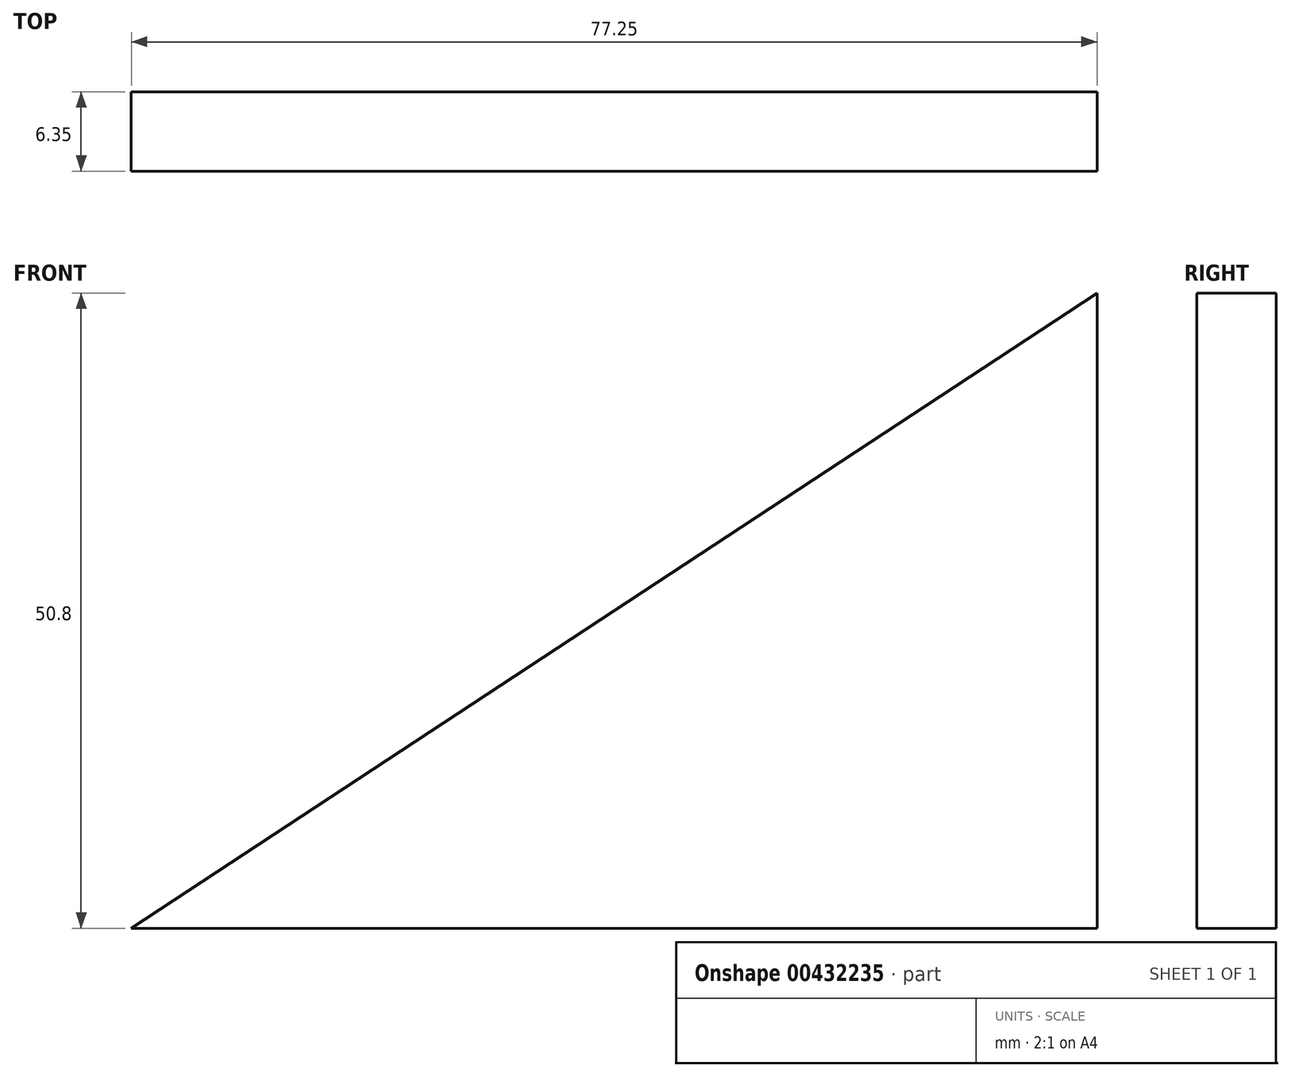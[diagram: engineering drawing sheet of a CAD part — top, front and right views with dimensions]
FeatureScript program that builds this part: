
annotation { "Feature Type Name" : "Feature", "Feature Type Description" : "" }
export const myFeature = defineFeature(function(context is Context, id is Id, definition is map)
    precondition{}
    {
        {
            var Q0;
            Q0=qCreatedBy(makeId("Front.planeOp"),FACE);
            var sketch = newSketch(context, id + "F0", { "sketchPlane" : qUnion([Q0])});
            skLineSegment(sketch, "E0", {"start": v(0, 0) * mm, "end": v(-77.25, 0) * mm});
            skLineSegment(sketch, "E1", {"start": v(0, 0) * mm, "end": v(0, 50.8) * mm});
            skLineSegment(sketch, "E2", {"start": v(0, 50.8) * mm, "end": v(-77.25, 0) * mm});
            skSolve(sketch);
        }
        {
            var Q0;
            Q0=makeQuery(id+"F0.imprint","IMPRINT",FACE,{"disambiguationData":[TD([[makeQuery(id+"F0.imprint","IMPRINT",EDGE,{"derivedFrom":sQuery(id+"F0.wireOp",EDGE,"E0")}),-1.0]])]});
            extrude(context, id + "F1", {"entities" : qUnion([Q0]), "depth" : 6.35 * mm});
        }
    });
